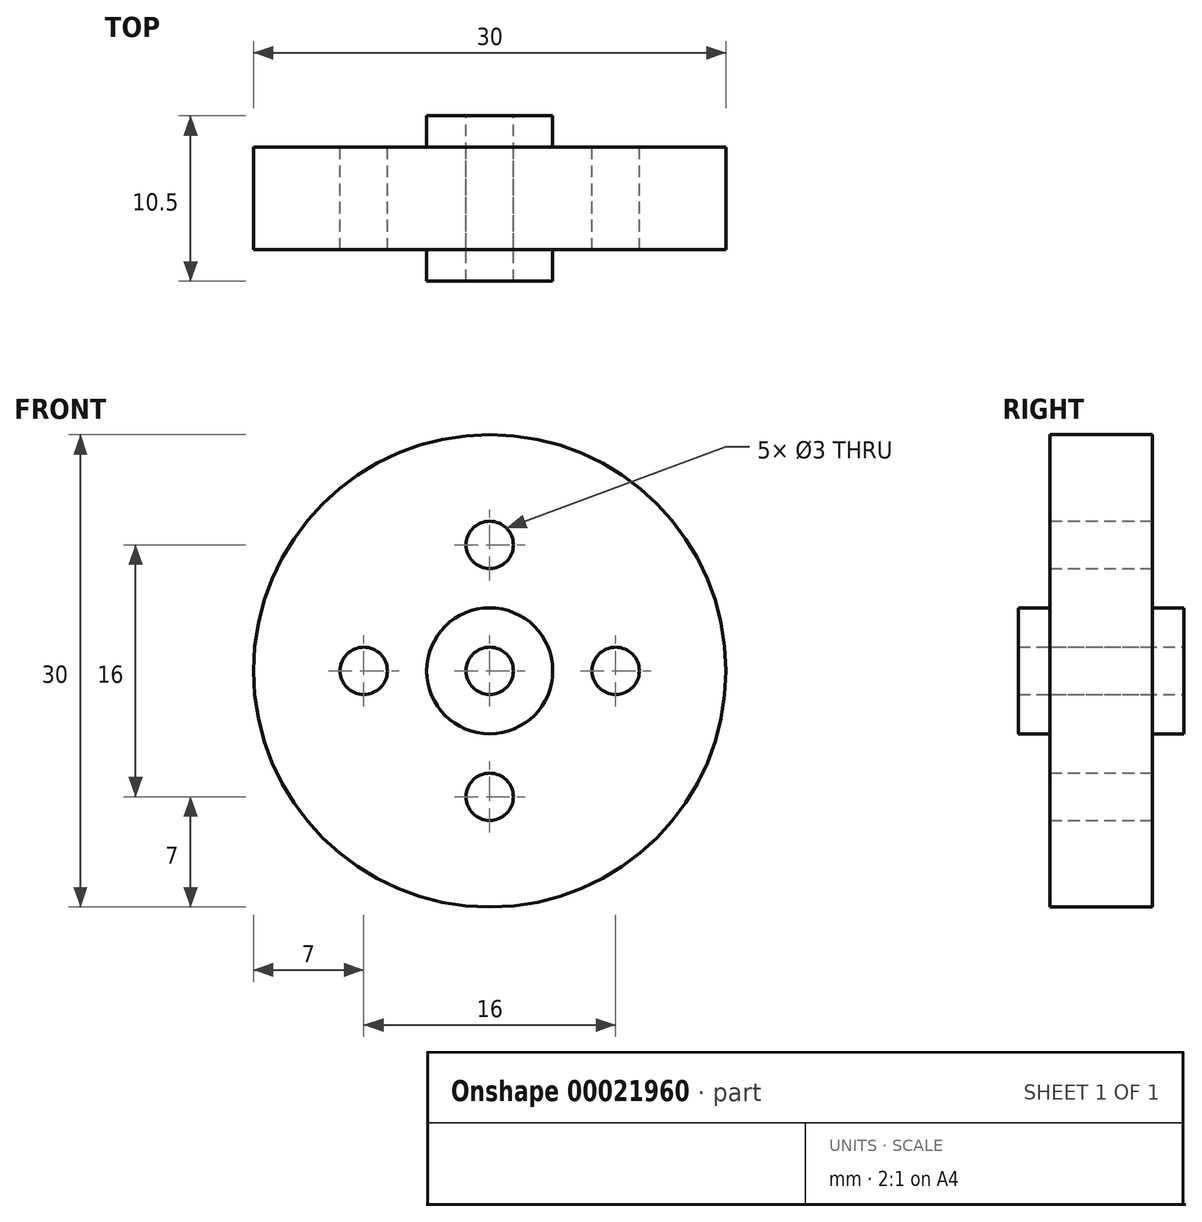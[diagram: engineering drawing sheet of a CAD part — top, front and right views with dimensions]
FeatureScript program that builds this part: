
annotation { "Feature Type Name" : "Feature", "Feature Type Description" : "" }
export const myFeature = defineFeature(function(context is Context, id is Id, definition is map)
    precondition{}
    {
        {
            var Q0;
            Q0=qCreatedBy(makeId("Front.planeOp"),FACE);
            var sketch = newSketch(context, id + "F0", { "sketchPlane" : qUnion([Q0])});
            skCircle(sketch, "E0", {"center": v(0, 0) * mm, "radius": 15 * mm});
            skCircle(sketch, "E1", {"center": v(0, 0) * mm, "radius": 1.5 * mm});
            skCircle(sketch, "E2", {"center": v(0, 8) * mm, "radius": 1.5 * mm});
            skCircle(sketch, "E3.1.0", {"center": v(-8, 0) * mm, "radius": 1.5 * mm});
            skCircle(sketch, "E3.2.0", {"center": v(0, -8) * mm, "radius": 1.5 * mm});
            skCircle(sketch, "E3.3.0", {"center": v(8, 0) * mm, "radius": 1.5 * mm});
            skCircle(sketch, "E4", {"center": v(0, 0) * mm, "radius": 4 * mm});
            skCircle(sketch, "E5", {"center": v(0, 0) * mm, "radius": 12 * mm});
            skSolve(sketch);
        }
        {
            var Q0;
            Q0 = qSketchRegion(id + "F0", true);
            var Q1;
            Q1=makeQuery(id+"F0.imprint","IMPRINT",FACE,{"disambiguationData":[TD([[makeQuery(id+"F0.imprint","IMPRINT",EDGE,{"derivedFrom":sQuery(id+"F0.wireOp",EDGE,"E2")}),-1.0]])]});
            var Q2;
            Q2=makeQuery(id+"F0.imprint","IMPRINT",FACE,{"disambiguationData":[TD([[makeQuery(id+"F0.imprint","IMPRINT",EDGE,{"derivedFrom":sQuery(id+"F0.wireOp",EDGE,"E1")}),-1.0]])]});
            extrude(context, id + "F1", {"entities" : qUnion([Q0, Q1, Q2]), "endBound" : BoundingType.SYMMETRIC, "depth" : 6.5 * mm});
        }
        {
            var Q0;
            Q0=makeQuery(id+"F0.imprint","IMPRINT",FACE,{"disambiguationData":[TD([[makeQuery(id+"F0.imprint","IMPRINT",EDGE,{"derivedFrom":sQuery(id+"F0.wireOp",EDGE,"E1")}),-1.0]])]});
            extrude(context, id + "F2", {"entities" : qUnion([Q0]), "operationType" : NewBodyOperationType.ADD, "endBound" : BoundingType.SYMMETRIC, "depth" : 10.5 * mm});
        }
    });
